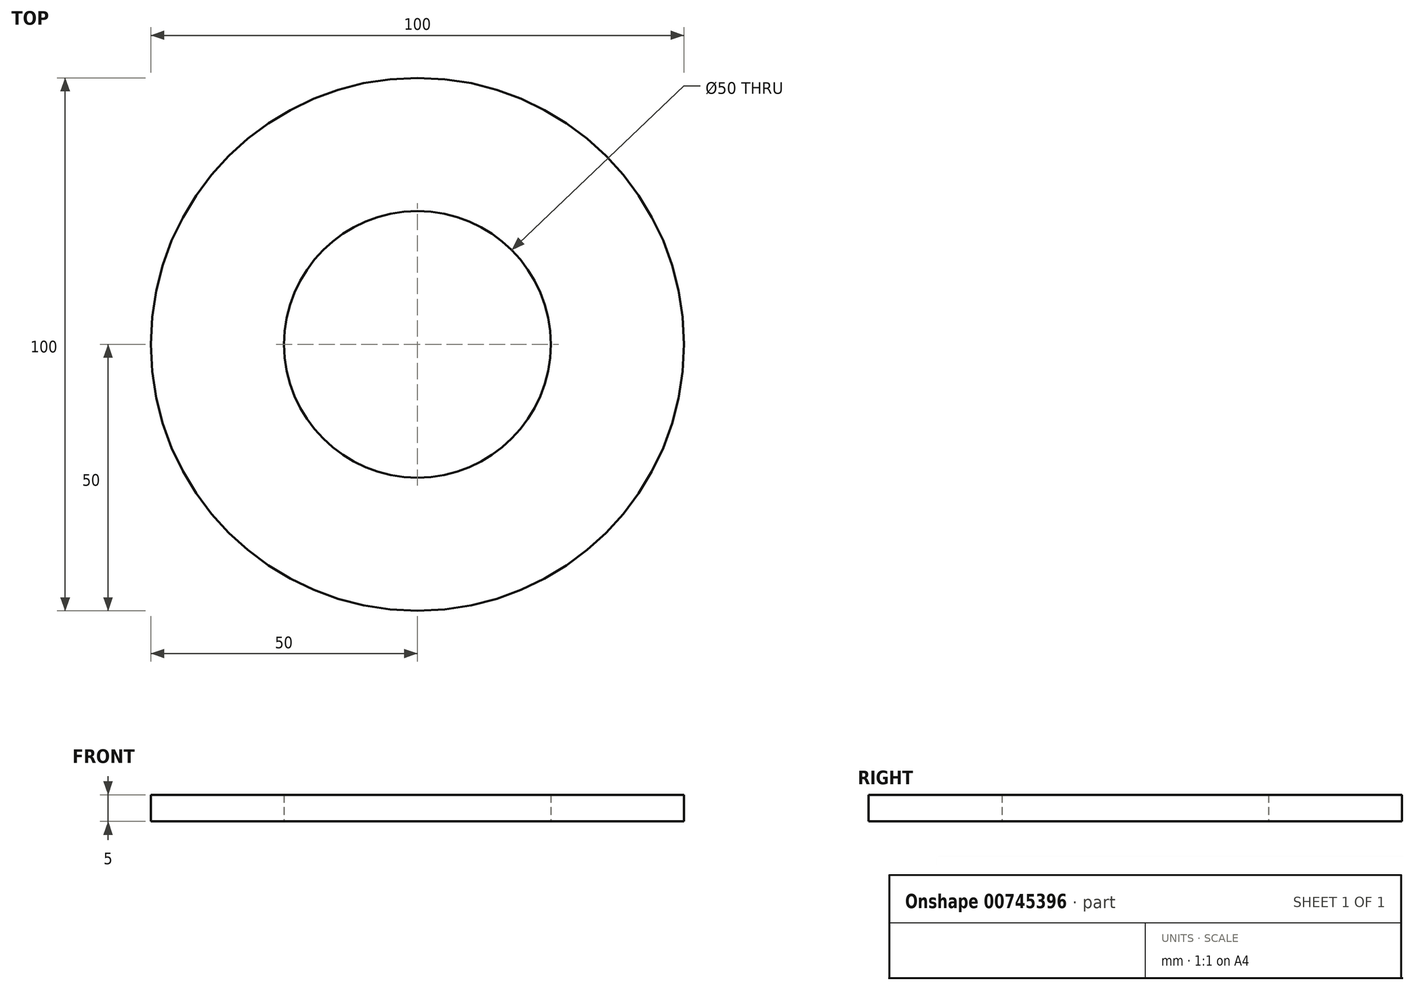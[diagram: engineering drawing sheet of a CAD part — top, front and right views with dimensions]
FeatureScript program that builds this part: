
annotation { "Feature Type Name" : "Feature", "Feature Type Description" : "" }
export const myFeature = defineFeature(function(context is Context, id is Id, definition is map)
    precondition{}
    {
        {
            var Q0;
            Q0=qCreatedBy(makeId("Top.planeOp"),FACE);
            var sketch = newSketch(context, id + "F0", { "sketchPlane" : qUnion([Q0])});
            skCircle(sketch, "E0", {"center": v(0, 0) * mm, "radius": 50 * mm});
            skCircle(sketch, "E1", {"center": v(0, 0) * mm, "radius": 25 * mm});
            skSolve(sketch);
        }
        {
            var Q0;
            Q0 = qSketchRegion(id + "F0", true);
            extrude(context, id + "F1", {"entities" : qUnion([Q0]), "depth" : 5 * mm, "offsetDistance" : 25 * mm});
        }
    });
